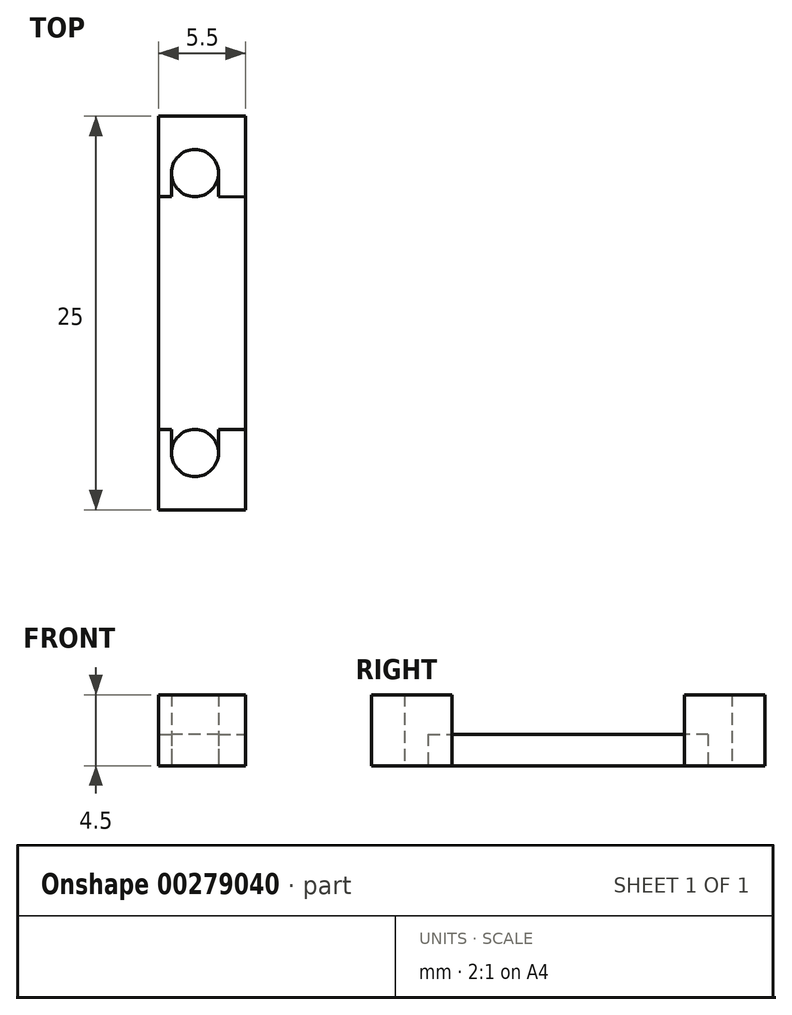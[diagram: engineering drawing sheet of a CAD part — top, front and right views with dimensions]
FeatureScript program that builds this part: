
annotation { "Feature Type Name" : "Feature", "Feature Type Description" : "" }
export const myFeature = defineFeature(function(context is Context, id is Id, definition is map)
    precondition{}
    {
        {
            var Q0;
            Q0=qCreatedBy(makeId("Top.planeOp"),FACE);
            var sketch = newSketch(context, id + "F0", { "sketchPlane" : qUnion([Q0])});
            skLineSegment(sketch, "E0.bottom", {"start": v(2.75, -12.5) * mm, "end": v(-2.75, -12.5) * mm});
            skLineSegment(sketch, "E0.top", {"start": v(2.75, 12.5) * mm, "end": v(-2.75, 12.5) * mm});
            skLineSegment(sketch, "E0.left", {"start": v(2.75, -12.5) * mm, "end": v(2.75, 12.5) * mm});
            skLineSegment(sketch, "E0.right", {"start": v(-2.75, -12.5) * mm, "end": v(-2.75, 12.5) * mm});
            skPoint(sketch, "E0.middle", {"position": v(0, 0) * mm});
            skLineSegment(sketch, "E1", {"start": v(-6.92, 8.9) * mm, "end": v(7.53, 8.9) * mm, "construction": true});
            skLineSegment(sketch, "E2", {"start": v(-5.28, -8.9) * mm, "end": v(7.25, -8.9) * mm, "construction": true});
            skLineSegment(sketch, "E3", {"start": v(1.05, 13.54) * mm, "end": v(1.05, -13.14) * mm, "construction": true});
            skCircle(sketch, "E4", {"center": v(-0.45, 8.9) * mm, "radius": 1.5 * mm});
            skCircle(sketch, "E5", {"center": v(-0.45, -8.9) * mm, "radius": 1.5 * mm});
            skLineSegment(sketch, "E6", {"start": v(-2.75, -7.4) * mm, "end": v(-1.95, -7.4) * mm});
            skLineSegment(sketch, "E7", {"start": v(-2.75, 7.4) * mm, "end": v(-1.95, 7.4) * mm});
            skLineSegment(sketch, "E8", {"start": v(-1.95, 8.9) * mm, "end": v(-1.95, 7.4) * mm});
            skLineSegment(sketch, "E9", {"start": v(1.05, 8.9) * mm, "end": v(1.05, 7.38) * mm});
            skLineSegment(sketch, "E10", {"start": v(-1.95, -8.9) * mm, "end": v(-1.95, -7.4) * mm});
            skLineSegment(sketch, "E11", {"start": v(1.05, -8.9) * mm, "end": v(1.05, -7.4) * mm});
            skLineSegment(sketch, "E12.trimOffspring", {"start": v(1.05, -7.4) * mm, "end": v(2.75, -7.4) * mm});
            skLineSegment(sketch, "E13.trimOffspring", {"start": v(1.05, 7.38) * mm, "end": v(2.75, 7.38) * mm});
            skSolve(sketch);
        }
        {
            var Q0;
            {var subQ4=sQuery(id+"F0.wireOp",EDGE,"E0.bottom");Q0=makeQuery(id+"F0.imprint","IMPRINT",FACE,{"disambiguationData":[TD([[makeQuery(id+"F0.imprint","IMPRINT",EDGE,{"derivedFrom":subQ4}),-1.0]])]});}
            var Q1;
            {var subQ3=sQuery(id+"F0.wireOp",EDGE,"E0.top");Q1=makeQuery(id+"F0.imprint","IMPRINT",FACE,{"disambiguationData":[TD([[makeQuery(id+"F0.imprint","IMPRINT",EDGE,{"derivedFrom":subQ3}),1.0]])]});}
            extrude(context, id + "F1", {"entities" : qUnion([Q0, Q1]), "depth" : 4.5 * mm});
        }
        {
            var Q0;
            {var subQ4=sQuery(id+"F0.wireOp",EDGE,"E6");Q0=makeQuery(id+"F0.imprint","IMPRINT",FACE,{"disambiguationData":[TD([[makeQuery(id+"F0.imprint","IMPRINT",EDGE,{"derivedFrom":subQ4}),1.0]])]});}
            extrude(context, id + "F2", {"entities" : qUnion([Q0]), "depth" : 2 * mm});
        }
    });
